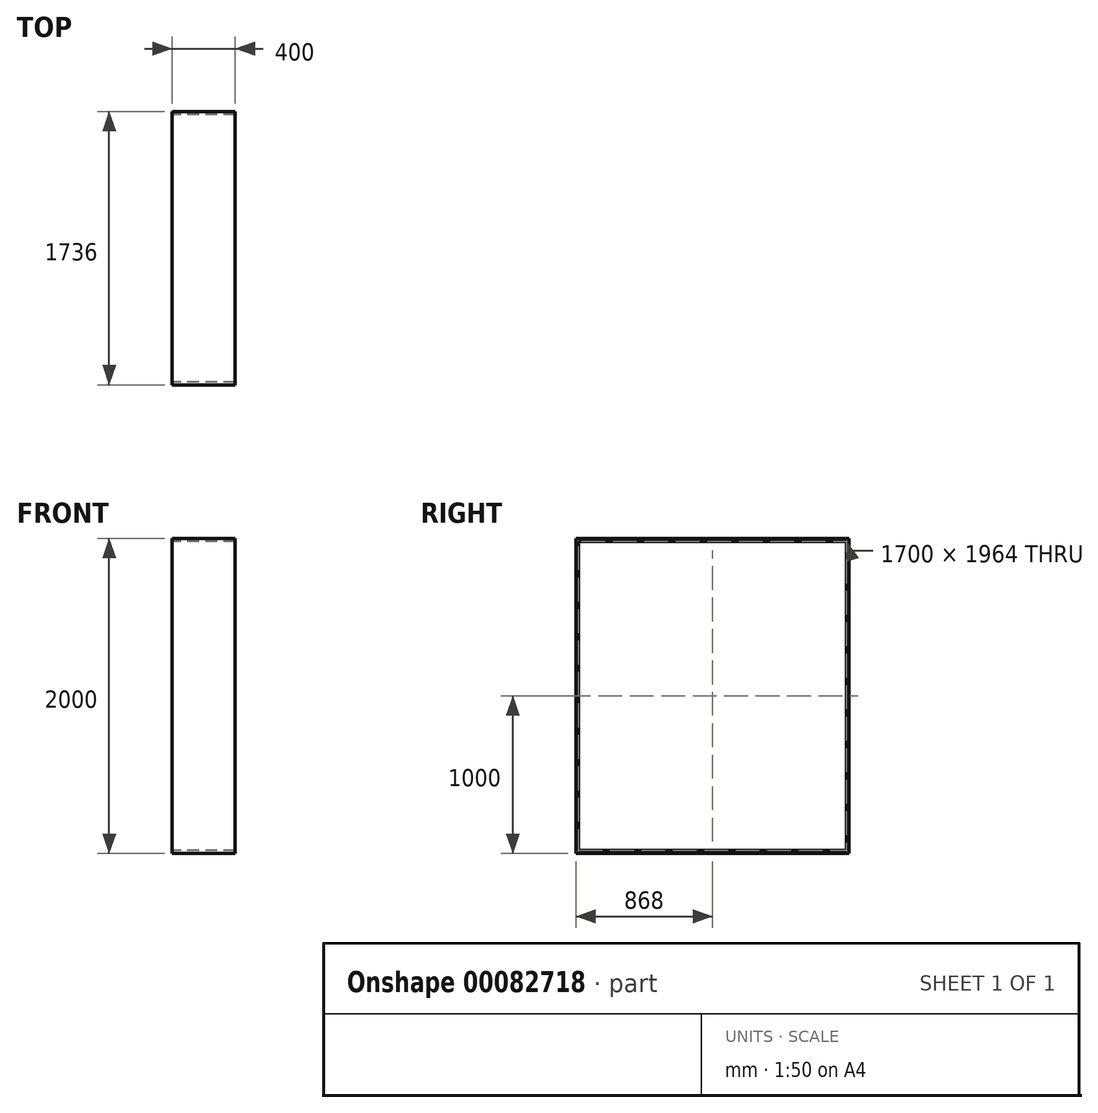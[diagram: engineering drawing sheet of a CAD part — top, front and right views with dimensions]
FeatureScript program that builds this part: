
annotation { "Feature Type Name" : "Feature", "Feature Type Description" : "" }
export const myFeature = defineFeature(function(context is Context, id is Id, definition is map)
    precondition{}
    {
        {
            var Q0;
            Q0=qCreatedBy(makeId("Right.planeOp"),FACE);
            var sketch = newSketch(context, id + "F0", { "sketchPlane" : qUnion([Q0])});
            skLineSegment(sketch, "E0.bottom", {"start": v(0, 0) * mm, "end": v(2630, 0) * mm});
            skLineSegment(sketch, "E0.top", {"start": v(0, 2900) * mm, "end": v(2630, 2900) * mm});
            skLineSegment(sketch, "E0.left", {"start": v(0, 0) * mm, "end": v(0, 2900) * mm});
            skLineSegment(sketch, "E0.right", {"start": v(2630, 0) * mm, "end": v(2630, 2900) * mm});
            skLineSegment(sketch, "E1.bottom", {"start": v(0, 0) * mm, "end": v(890, 0) * mm});
            skLineSegment(sketch, "E1.top", {"start": v(0, 2110) * mm, "end": v(890, 2110) * mm});
            skLineSegment(sketch, "E1.left", {"start": v(0, 0) * mm, "end": v(0, 2110) * mm});
            skLineSegment(sketch, "E1.right", {"start": v(890, 0) * mm, "end": v(890, 2110) * mm});
            skLineSegment(sketch, "E2.bottom", {"start": v(2600, 120) * mm, "end": v(900, 120) * mm});
            skLineSegment(sketch, "E2.top", {"start": v(2600, 138) * mm, "end": v(900, 138) * mm});
            skLineSegment(sketch, "E2.left", {"start": v(2600, 120) * mm, "end": v(2600, 138) * mm});
            skLineSegment(sketch, "E2.right", {"start": v(900, 120) * mm, "end": v(900, 138) * mm});
            skLineSegment(sketch, "E3.bottom", {"start": v(2600, 2120) * mm, "end": v(900, 2120) * mm});
            skLineSegment(sketch, "E3.top", {"start": v(2600, 2102) * mm, "end": v(900, 2102) * mm});
            skLineSegment(sketch, "E3.left", {"start": v(2600, 2120) * mm, "end": v(2600, 2102) * mm});
            skLineSegment(sketch, "E3.right", {"start": v(900, 2120) * mm, "end": v(900, 2102) * mm});
            skSolve(sketch);
        }
        {
            var Q0;
            Q0=makeQuery(id+"F0.imprint","IMPRINT",FACE,{"disambiguationData":[TD([[makeQuery(id+"F0.imprint","IMPRINT",EDGE,{"derivedFrom":sQuery(id+"F0.wireOp",EDGE,"E2.bottom")}),-1.0]])]});
            var Q1;
            Q1=makeQuery(id+"F0.imprint","IMPRINT",FACE,{"disambiguationData":[TD([[makeQuery(id+"F0.imprint","IMPRINT",EDGE,{"derivedFrom":sQuery(id+"F0.wireOp",EDGE,"E3.bottom")}),1.0]])]});
            extrude(context, id + "F1", {"entities" : qUnion([Q0, Q1]), "depth" : 400 * mm});
        }
        {
            var Q0;
            Q0=makeQuery(id+"F1.opExtrude","CAP_FACE",FACE,{"disambiguationData":[OSD([sQuery(id+"F0.wireOp",EDGE,"E2.bottom"),sQuery(id+"F0.wireOp",EDGE,"E2.top"),sQuery(id+"F0.wireOp",EDGE,"E2.left"),sQuery(id+"F0.wireOp",EDGE,"E2.right")])],"isStart":false});
            var sketch = newSketch(context, id + "F2", { "sketchPlane" : qUnion([Q0])});
            skLineSegment(sketch, "E4.bottom", {"start": v(2600, 120) * mm, "end": v(2618, 120) * mm});
            skLineSegment(sketch, "E4.top", {"start": v(2600, 2120) * mm, "end": v(2618, 2120) * mm});
            skLineSegment(sketch, "E4.left", {"start": v(2600, 120) * mm, "end": v(2600, 2120) * mm});
            skLineSegment(sketch, "E4.right", {"start": v(2618, 120) * mm, "end": v(2618, 2120) * mm});
            skLineSegment(sketch, "E5.bottom", {"start": v(900, 120) * mm, "end": v(882, 120) * mm});
            skLineSegment(sketch, "E5.top", {"start": v(900, 2120) * mm, "end": v(882, 2120) * mm});
            skLineSegment(sketch, "E5.left", {"start": v(900, 120) * mm, "end": v(900, 2120) * mm});
            skLineSegment(sketch, "E5.right", {"start": v(882, 120) * mm, "end": v(882, 2120) * mm});
            skSolve(sketch);
        }
        {
            var Q0;
            {var subQ1=sQuery(id+"F2.wireOp",EDGE,"E5.bottom");Q0=makeQuery(id+"F2.imprint","IMPRINT",FACE,{"disambiguationData":[TD([[makeQuery(id+"F2.imprint","IMPRINT",EDGE,{"derivedFrom":subQ1}),-1.0]])]});}
            var Q1;
            {var subQ1=sQuery(id+"F2.wireOp",EDGE,"E4.bottom");Q1=makeQuery(id+"F2.imprint","IMPRINT",FACE,{"disambiguationData":[TD([[makeQuery(id+"F2.imprint","IMPRINT",EDGE,{"derivedFrom":subQ1}),1.0]])]});}
            extrude(context, id + "F3", {"entities" : qUnion([Q0, Q1]), "operationType" : NewBodyOperationType.ADD, "oppositeDirection" : true, "depth" : 400 * mm});
        }
    });
